# Revit family: Table-Casual-Naughtone-Dalby_SQ_Cafe
name_source: partatom
category: Furniture
revit_build: Autodesk Revit 2015 (Build: 20150704_0715(x64)
units: mm (PartAtom-declared; Revit-internal decimal feet)

## types (2) — shared parameters
AdditionalMaterials = Additional material and finish options available. Please contact Naughtone direct for further information.
Assembly Code = E2020
AssetType = Movable
BIMObjectName = Table-Casual-Naughtone-Dalby_SQ_Cafe
BarCode = 0.000000
Category = 40.50.21.58 : Occasional Tables
CodePerformance = FISP Certified; ISO14001 Certified
Color = White
ComponentDescription = The Dalby table will inject warmth and quality into an interior without raising any eyebrows. Dalby provides a practical, robust surface and maximised leg positions for clear, useable access all round the table.
Constituents = Wood Top; Solid Oak frame
Description = Dalby Square Cafe Table
DurationUnit = Years
ExpectedLife = 15-20
Finish = Polyster powder coat; various top finishes available
Keynote = 40.50.21.58
Manufacturer = Naughtone
ManufacturerAddressUK = 201 Pannal Business Park, Station Road, Harrogate, HG3 1JL
Material = MFMDF Top; Solid Oak Legs
ModelReference = Dalby Square Cafe Table
NBSReference = 40.50.21.58
NominalHeight = 750 mm  [stored 2.46063 ft]
Product URL = http://www.naughtone.com
ProductInformation = http://www.naughtone.com
ReplacementCost = 0.00
SerialNumber = 0.000000
Shape = Rectangular
SustainabilityPerformance = 89.64% reusable content
TagNumber = 0.000000
TypeName = Table-Casual-Naughtone-Dalby_SQ_Cafe
URL = http://www.naughtone.com
Uniclass2015 = 40.50.21.58
Version = 1
WarrantyDescription = 5 year warranty
WarrantyDurationLabor = 5
WarrantyDurationParts = 5
WarrantyDurationUnit = Years
_current revision = 1
_distributed by = www.bimbox.co.uk
zero-valued in all types: Cost, _BIMspec_GUID

## per-type parameters (varying)
| type | AssetIdentifier | Model | ModelNumber | Name | NominalLength | NominalWidth | Type Comments |
| 650mmx650mmx750mm | DAL-650-SQ | DAL-650-SQ | DAL-650-SQ | 650mmx650mmx750mm, Dalby Square Cafe Table | 650 mm  [stored 2.13255 ft] | 650 mm  [stored 2.13255 ft] | 650x650x750 |
| 850mmx850mmx750mm | DAL-850-SQ | DAL-850-SQ | DAL-850-SQ | 850mmx850mmx750mm, Dalby Square Cafe Table | 850 mm  [stored 2.78871 ft] | 850 mm  [stored 2.78871 ft] | 850x850x750 |

note: column(s) folded — value = type name in every type: Size

note: [stored X ft] marks values corroborated as IEEE doubles in the binary element streams (Revit-internal decimal feet)

## geometry (parser evidence)
native form markers: Sweep x4
no freeform markers — native parametric forms only
